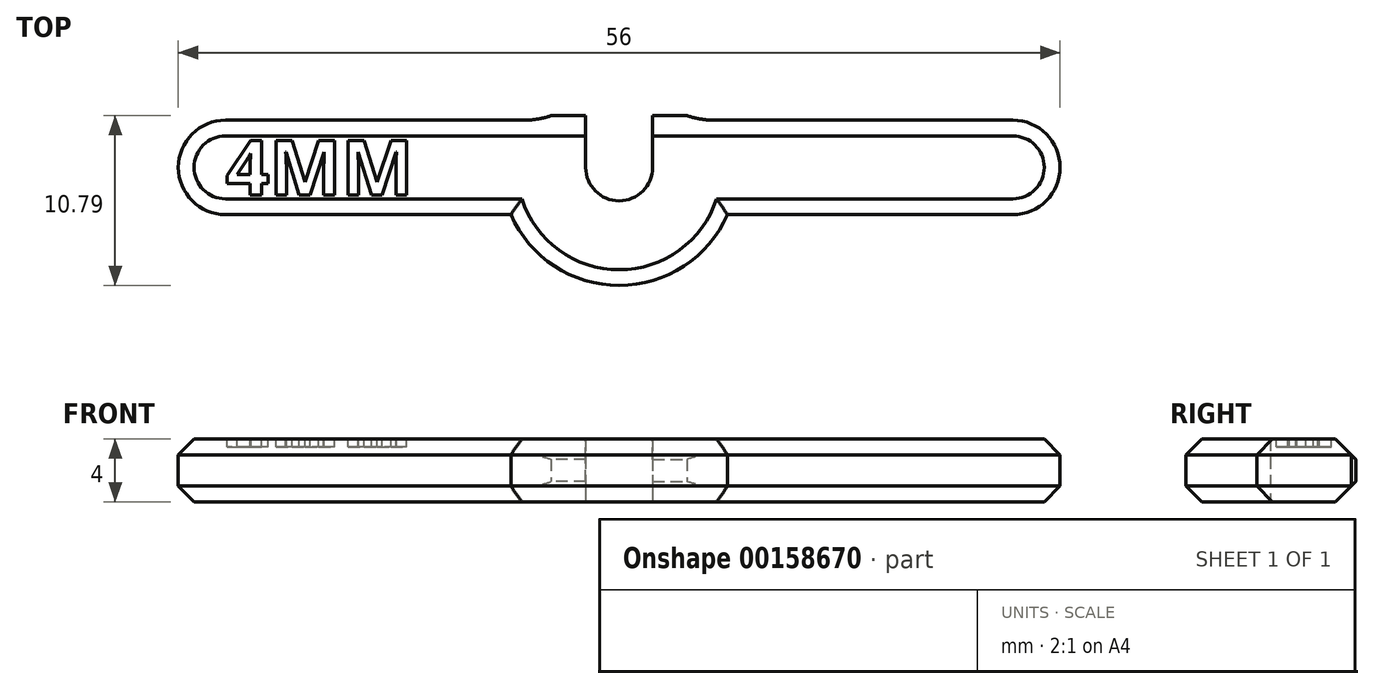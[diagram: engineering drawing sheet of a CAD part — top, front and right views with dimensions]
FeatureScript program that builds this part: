
annotation { "Feature Type Name" : "Feature", "Feature Type Description" : "" }
export const myFeature = defineFeature(function(context is Context, id is Id, definition is map)
    precondition{}
    {
        {
            var Q0;
            Q0=qCreatedBy(makeId("Top.planeOp"),FACE);
            var sketch = newSketch(context, id + "F0", { "sketchPlane" : qUnion([Q0])});
            skArc(sketch, "E0", {"start": v(-2.12, 0) * mm, "mid": v(0, -2.12) * mm, "end": v(2.12, 0) * mm});
            skArc(sketch, "E1", {"start": v(-2.5, 4.33) * mm, "mid": v(-3.32, 3.74) * mm, "end": v(-4, 3) * mm});
            skLineSegment(sketch, "E2", {"start": v(2.12, 0) * mm, "end": v(2.12, 4.11) * mm});
            skLineSegment(sketch, "E3", {"start": v(-2.12, 0) * mm, "end": v(-2.12, 4.11) * mm});
            skPoint(sketch, "E4.visualSharp", {"position": v(-2.12, 4.53) * mm});
            skArc(sketch, "E4.filletArc", {"start": v(-2.12, 4.11) * mm, "mid": v(-2.25, 4.33) * mm, "end": v(-2.5, 4.33) * mm});
            skPoint(sketch, "E5.visualSharp", {"position": v(2.12, 4.53) * mm});
            skArc(sketch, "E5.filletArc", {"start": v(2.5, 4.33) * mm, "mid": v(2.25, 4.33) * mm, "end": v(2.12, 4.11) * mm});
            skLineSegment(sketch, "E6.0", {"start": v(-4, 3) * mm, "end": v(-25, 3) * mm});
            skLineSegment(sketch, "E7.0", {"start": v(-4, -3) * mm, "end": v(-25, -3) * mm});
            skArc(sketch, "E8", {"start": v(-25, 3) * mm, "mid": v(-28, 0) * mm, "end": v(-25, -3) * mm});
            skPoint(sketch, "E9.start.orphan", {"position": v(-5, 0) * mm});
            skArc(sketch, "E10.trimOffspring", {"start": v(-4, -3) * mm, "mid": v(3.74, -3.32) * mm, "end": v(2.5, 4.33) * mm});
            skLineSegment(sketch, "E11.MirrorCS", {"start": v(4, 3) * mm, "end": v(25, 3) * mm});
            skLineSegment(sketch, "E12.MirrorCS", {"start": v(4, -3) * mm, "end": v(25, -3) * mm});
            skArc(sketch, "E13.MirrorCS", {"start": v(25, 3) * mm, "mid": v(28, 0) * mm, "end": v(25, -3) * mm});
            skSolve(sketch);
        }
        {
            var Q0;
            Q0 = qSketchRegion(id + "F0", true);
            extrude(context, id + "F1", {"entities" : qUnion([Q0]), "depth" : 4 * mm});
        }
        {
            var Q0;
            Q0=makeQuery(id+"F1.opExtrude","SWEPT_EDGE",EDGE,{"disambiguationData":[OSD([sQuery(id+"F0.wireOp",EDGE,"E7.0"),sQuery(id+"F0.wireOp",EDGE,"E10.trimOffspring")])]});
            var Q1;
            Q1=makeQuery(id+"F1.opExtrude","SWEPT_EDGE",EDGE,{"disambiguationData":[OSD([sQuery(id+"F0.wireOp",EDGE,"E10.trimOffspring"),sQuery(id+"F0.wireOp",EDGE,"E12.MirrorCS")])]});
            var Q2;
            Q2=makeQuery(id+"F1.opExtrude","SWEPT_EDGE",EDGE,{"disambiguationData":[OSD([sQuery(id+"F0.wireOp",EDGE,"E1"),sQuery(id+"F0.wireOp",EDGE,"E6.0")])]});
            var Q3;
            Q3=makeQuery(id+"F1.opExtrude","SWEPT_EDGE",EDGE,{"disambiguationData":[OSD([sQuery(id+"F0.wireOp",EDGE,"E10.trimOffspring"),sQuery(id+"F0.wireOp",EDGE,"E11.MirrorCS")])]});
            fillet(context, id + "F2", {"entities" : qUnion([Q0, Q1, Q2, Q3]), "radius" : 5 * mm, "tangentPropagation" : true, "allowEdgeOverflow" : false});
        }
        {
            var Q0;
            Q0=makeQuery(id+"F1.opExtrude","CAP_EDGE",EDGE,{"disambiguationData":[OSD([sQuery(id+"F0.wireOp",EDGE,"E7.0")])],"isStart":false});
            var Q1;
            Q1=makeQuery(id+"F1.opExtrude","CAP_EDGE",EDGE,{"disambiguationData":[OSD([sQuery(id+"F0.wireOp",EDGE,"E7.0")])],"isStart":true});
            var Q2;
            Q2=makeQuery(id+"F1.opExtrude","CAP_EDGE",EDGE,{"disambiguationData":[OSD([sQuery(id+"F0.wireOp",EDGE,"E6.0")])],"isStart":false});
            var Q3;
            Q3=makeQuery(id+"F1.opExtrude","CAP_EDGE",EDGE,{"disambiguationData":[OSD([sQuery(id+"F0.wireOp",EDGE,"E11.MirrorCS")])],"isStart":false});
            var Q4;
            Q4=makeQuery(id+"F1.opExtrude","CAP_EDGE",EDGE,{"disambiguationData":[OSD([sQuery(id+"F0.wireOp",EDGE,"E11.MirrorCS")])],"isStart":true});
            var Q5;
            Q5=makeQuery(id+"F1.opExtrude","CAP_EDGE",EDGE,{"disambiguationData":[OSD([sQuery(id+"F0.wireOp",EDGE,"E6.0")])],"isStart":true});
            var Q6;
            Q6=makeQuery(id+"F1.opExtrude","CAP_EDGE",EDGE,{"disambiguationData":[OSD([sQuery(id+"F0.wireOp",EDGE,"E8")])],"isStart":false});
            var Q7;
            Q7=makeQuery(id+"F1.opExtrude","CAP_EDGE",EDGE,{"disambiguationData":[OSD([sQuery(id+"F0.wireOp",EDGE,"E8")])],"isStart":true});
            chamfer(context, id + "F3", {"entities" : qUnion([Q0, Q1, Q2, Q3, Q4, Q5, Q6, Q7]), "width" : 1 * mm});
        }
        {
            var Q0;
            Q0=makeQuery(id+"F1.opExtrude","CAP_EDGE",EDGE,{"disambiguationData":[OSD([sQuery(id+"F0.wireOp",EDGE,"E13.MirrorCS")])],"isStart":false});
            var Q1;
            Q1=makeQuery(id+"F1.opExtrude","CAP_EDGE",EDGE,{"disambiguationData":[OSD([sQuery(id+"F0.wireOp",EDGE,"E13.MirrorCS")])],"isStart":true});
            var Q2;
            {var subQ0=sQuery(id+"F0.wireOp",EDGE,"E7.0");Q2=makeQuery(id+"F3.opChamfer","BLEND_EDGE",EDGE,{"blendedFrom":[makeQuery(id+"F1.opExtrude","CAP_EDGE",EDGE,{"disambiguationData":[OSD([subQ0])],"isStart":true}),makeQuery(id+"F1.opExtrude","CAP_EDGE",EDGE,{"disambiguationData":[OSD([subQ0])],"isStart":false})],"blendedInto":[]});}
            var Q3;
            {var subQ0=sQuery(id+"F0.wireOp",EDGE,"E11.MirrorCS");Q3=makeQuery(id+"F3.opChamfer","BLEND_EDGE",EDGE,{"blendedFrom":[makeQuery(id+"F1.opExtrude","CAP_EDGE",EDGE,{"disambiguationData":[OSD([subQ0])],"isStart":true}),makeQuery(id+"F1.opExtrude","CAP_EDGE",EDGE,{"disambiguationData":[OSD([subQ0])],"isStart":false})],"blendedInto":[]});}
            var Q4;
            {var subQ0=sQuery(id+"F0.wireOp",EDGE,"E6.0");Q4=makeQuery(id+"F3.opChamfer","BLEND_EDGE",EDGE,{"blendedFrom":[makeQuery(id+"F1.opExtrude","CAP_EDGE",EDGE,{"disambiguationData":[OSD([subQ0])],"isStart":true}),makeQuery(id+"F1.opExtrude","CAP_EDGE",EDGE,{"disambiguationData":[OSD([subQ0])],"isStart":false})],"blendedInto":[]});}
            chamfer(context, id + "F4", {"entities" : qUnion([Q0, Q1, Q2, Q3, Q4]), "width" : 1 * mm, "tangentPropagation" : true});
        }
        {
            var Q0;
            Q0=makeQuery(id+"F3.opChamfer","SPLIT",FACE,{"disambiguationData":[OD(1.0)],"derivedFrom":makeQuery(id+"F1.opExtrude","CAP_FACE",FACE,{"disambiguationData":[OSD([sQuery(id+"F0.wireOp",EDGE,"E0"),sQuery(id+"F0.wireOp",EDGE,"E1"),sQuery(id+"F0.wireOp",EDGE,"E2"),sQuery(id+"F0.wireOp",EDGE,"E3"),sQuery(id+"F0.wireOp",EDGE,"E4.filletArc"),sQuery(id+"F0.wireOp",EDGE,"E5.filletArc"),sQuery(id+"F0.wireOp",EDGE,"E6.0"),sQuery(id+"F0.wireOp",EDGE,"E7.0"),sQuery(id+"F0.wireOp",EDGE,"E8"),sQuery(id+"F0.wireOp",EDGE,"E10.trimOffspring"),sQuery(id+"F0.wireOp",EDGE,"E11.MirrorCS"),sQuery(id+"F0.wireOp",EDGE,"E12.MirrorCS"),sQuery(id+"F0.wireOp",EDGE,"E13.MirrorCS")])],"isStart":false})});
            var sketch = newSketch(context, id + "F5", { "sketchPlane" : qUnion([Q0])});
            skText(sketch, "E14", { "text": "4MM", "fontName": "OpenSans-Bold.ttf"});
            const initialGuessF5  = {"E14": [-0.025, -0.00175, 1, 0, 0.0035]};
            skSetInitialGuess(sketch, initialGuessF5);
            skSolve(sketch);
        }
        {
            var Q0;
            Q0 = qSketchRegion(id + "F5", true);
            extrude(context, id + "F6", {"entities" : qUnion([Q0]), "operationType" : NewBodyOperationType.REMOVE, "oppositeDirection" : true, "depth" : .5 * mm});
        }
        {
            var Q0;
            {var subQ0=sQuery(id+"F0.wireOp",EDGE,"E7.0");var subQ1=sQuery(id+"F0.wireOp",EDGE,"E0");var subQ2=sQuery(id+"F0.wireOp",EDGE,"E8");var subQ3=sQuery(id+"F0.wireOp",EDGE,"E3");var subQ4=sQuery(id+"F0.wireOp",EDGE,"E6.0");Q0=makeQuery(id+"F6.boolean.opBoolean","SPLIT",FACE,{"disambiguationData":[TD([makeQuery(id+"F1.opExtrude","SWEPT_FACE",FACE,{"disambiguationData":[OSD([subQ1])]})])],"derivedFrom":makeQuery(id+"F3.opChamfer","SPLIT",FACE,{"disambiguationData":[OD(1.0)],"derivedFrom":makeQuery(id+"F1.opExtrude","CAP_FACE",FACE,{"disambiguationData":[OSD([subQ1,sQuery(id+"F0.wireOp",EDGE,"E1"),sQuery(id+"F0.wireOp",EDGE,"E2"),subQ3,sQuery(id+"F0.wireOp",EDGE,"E4.filletArc"),sQuery(id+"F0.wireOp",EDGE,"E5.filletArc"),subQ4,subQ0,subQ2,sQuery(id+"F0.wireOp",EDGE,"E10.trimOffspring"),sQuery(id+"F0.wireOp",EDGE,"E11.MirrorCS"),sQuery(id+"F0.wireOp",EDGE,"E12.MirrorCS"),sQuery(id+"F0.wireOp",EDGE,"E13.MirrorCS")])],"isStart":false})})});}
            var sketch = newSketch(context, id + "F7", { "sketchPlane" : qUnion([Q0])});
            skCircle(sketch, "E15", {"center": v(0, 0) * mm, "radius": 7.5 * mm});
            skCircle(sketch, "E16", {"center": v(0, 0) * mm, "radius": 2.12 * mm});
            skLineSegment(sketch, "E17", {"start": v(-2.12, 0) * mm, "end": v(-7.5, 0) * mm});
            skLineSegment(sketch, "E18", {"start": v(2.12, 0) * mm, "end": v(7.5, 0) * mm});
            skSolve(sketch);
        }
        {
            var Q0;
            {var subQ0=sQuery(id+"F7.wireOp",EDGE,"E17");Q0=makeQuery(id+"F7.imprint","IMPRINT",FACE,{"disambiguationData":[TD([[makeQuery(id+"F7.imprint","IMPRINT",EDGE,{"derivedFrom":subQ0}),1.0]])]});}
            var Q1;
            {var subQ0=sQuery(id+"F7.wireOp",EDGE,"E18");Q1=makeQuery(id+"F7.imprint","IMPRINT",FACE,{"disambiguationData":[TD([[makeQuery(id+"F7.imprint","IMPRINT",EDGE,{"derivedFrom":subQ0}),-1.0]])]});}
            var Q2;
            Q2=makeQuery(id+"F3.opChamfer","SPLIT",FACE,{"disambiguationData":[OD(1.0)],"derivedFrom":makeQuery(id+"F1.opExtrude","CAP_FACE",FACE,{"disambiguationData":[OSD([sQuery(id+"F0.wireOp",EDGE,"E0"),sQuery(id+"F0.wireOp",EDGE,"E1"),sQuery(id+"F0.wireOp",EDGE,"E2"),sQuery(id+"F0.wireOp",EDGE,"E3"),sQuery(id+"F0.wireOp",EDGE,"E4.filletArc"),sQuery(id+"F0.wireOp",EDGE,"E5.filletArc"),sQuery(id+"F0.wireOp",EDGE,"E6.0"),sQuery(id+"F0.wireOp",EDGE,"E7.0"),sQuery(id+"F0.wireOp",EDGE,"E8"),sQuery(id+"F0.wireOp",EDGE,"E10.trimOffspring"),sQuery(id+"F0.wireOp",EDGE,"E11.MirrorCS"),sQuery(id+"F0.wireOp",EDGE,"E12.MirrorCS"),sQuery(id+"F0.wireOp",EDGE,"E13.MirrorCS")])],"isStart":true})});
            extrude(context, id + "F8", {"entities" : qUnion([Q0, Q1]), "operationType" : NewBodyOperationType.ADD, "endBound" : BoundingType.UP_TO_SURFACE, "oppositeDirection" : true, "endBoundEntityFace" : qUnion([Q2]), "depth" : 25 * mm});
        }
        {
            var Q0;
            Q0=makeQuery(id+"F8.opExtrude","CAP_EDGE",EDGE,{"disambiguationData":[OSD([sQuery(id+"F7.wireOp",EDGE,"E15")])],"isStart":true});
            var Q1;
            Q1=makeQuery(id+"F8.opExtrude","CAP_EDGE",EDGE,{"disambiguationData":[OSD([sQuery(id+"F7.wireOp",EDGE,"E15")])],"isStart":false});
            chamfer(context, id + "F9", {"entities" : qUnion([Q0, Q1]), "width" : 1 * mm, "tangentPropagation" : true});
        }
    });
